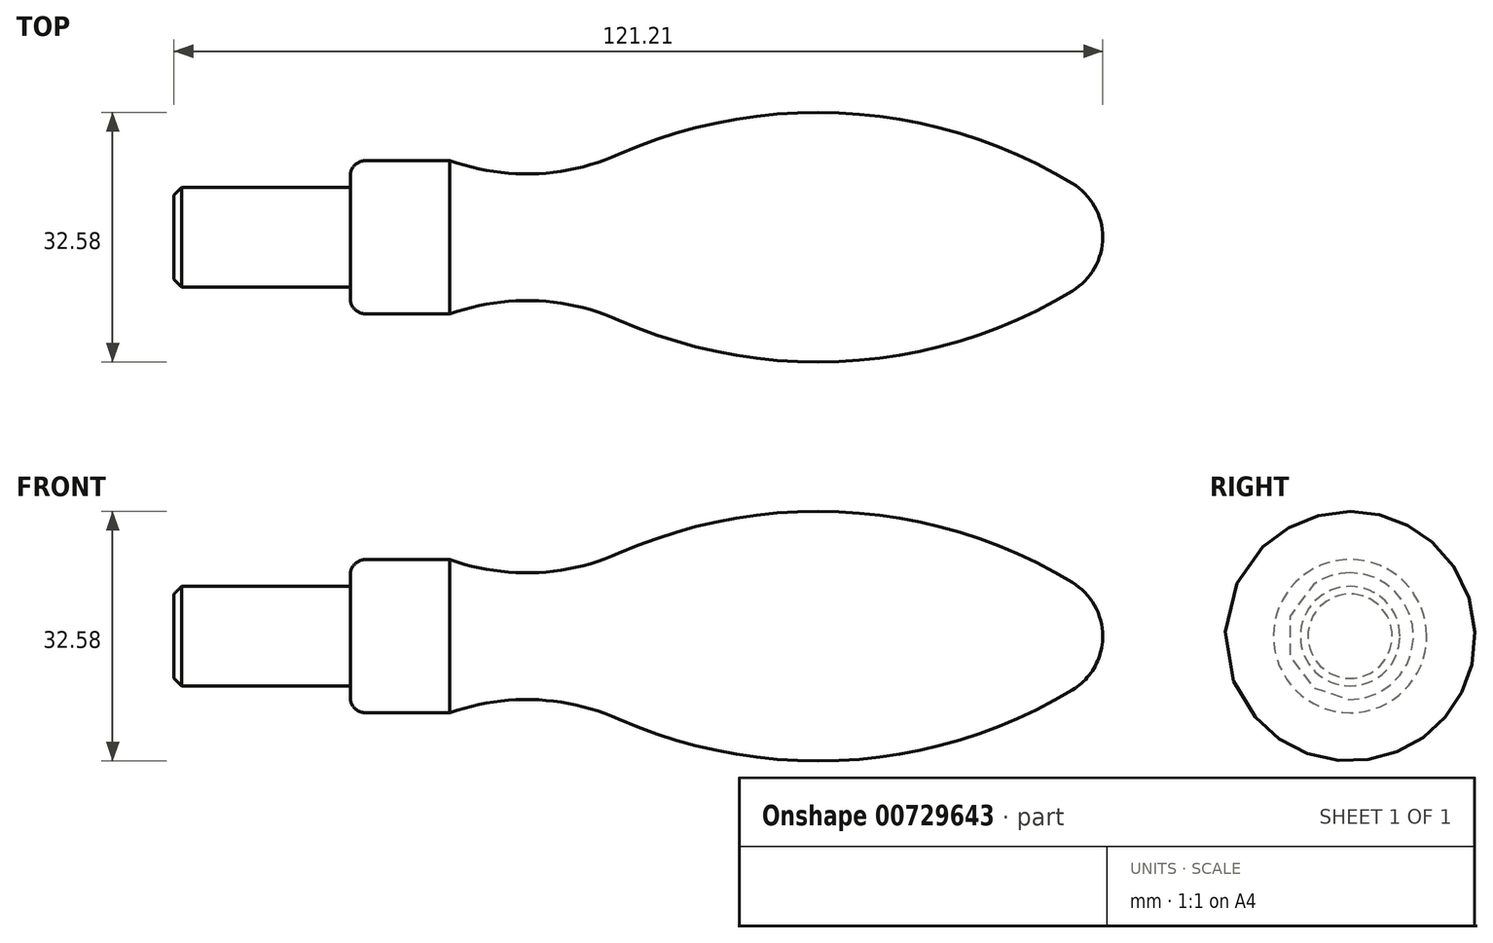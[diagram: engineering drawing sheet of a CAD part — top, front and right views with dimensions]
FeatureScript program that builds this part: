
annotation { "Feature Type Name" : "Feature", "Feature Type Description" : "" }
export const myFeature = defineFeature(function(context is Context, id is Id, definition is map)
    precondition{}
    {
        {
            var Q0;
            Q0=qCreatedBy(makeId("Front.planeOp"),FACE);
            var sketch = newSketch(context, id + "F0", { "sketchPlane" : qUnion([Q0])});
            skLineSegment(sketch, "E0", {"start": v(-68.37, 0) * mm, "end": v(0, 0) * mm, "construction": true});
            skLineSegment(sketch, "E1", {"start": v(0, 0) * mm, "end": v(23, -38) * mm, "construction": true});
            skLineSegment(sketch, "E2", {"start": v(0, 0) * mm, "end": v(0, -10) * mm});
            skLineSegment(sketch, "E3", {"start": v(0, -10) * mm, "end": v(13, -10) * mm});
            skLineSegment(sketch, "E4", {"start": v(61, 0) * mm, "end": v(61, 47.98) * mm, "construction": true});
            skLineSegment(sketch, "E5", {"start": v(90, 0) * mm, "end": v(90, 26.15) * mm, "construction": true});
            skArc(sketch, "E6", {"start": v(35.02, -10.8) * mm, "mid": v(24.09, -8.29) * mm, "end": v(13, -10) * mm});
            skArc(sketch, "E7", {"start": v(35.02, -10.8) * mm, "mid": v(65.1, -16.16) * mm, "end": v(94.25, -7.02) * mm});
            skArc(sketch, "E8", {"start": v(94.25, -7.02) * mm, "mid": v(97.15, -4.03) * mm, "end": v(98.2, 0) * mm});
            skLineSegment(sketch, "E9", {"start": v(0, 0) * mm, "end": v(98.2, 0) * mm, "construction": true});
            skLineSegment(sketch, "E10", {"start": v(0, 0) * mm, "end": v(98.2, 0) * mm});
            skSolve(sketch);
        }
        {
            var Q0;
            Q0 = qSketchRegion(id + "F0", true);
            var Q1;
            Q1=sQuery(id+"F0.wireOp",EDGE,"E0");
            revolve(context, id + "F1", {"surfaceOperationType" : NewSurfaceOperationType.NEW, "entities" : qUnion([Q0]), "axis" : qUnion([Q1]), "revolveType" : RevolveType.FULL});
        }
        {
            var Q0;
            Q0=makeQuery(id+"F1.opRevolve","SWEPT_FACE",FACE,{"disambiguationData":[OSD([sQuery(id+"F0.wireOp",EDGE,"E2")])]});
            var sketch = newSketch(context, id + "F2", { "sketchPlane" : qUnion([Q0])});
            skCircle(sketch, "E11", {"center": v(0, 0) * mm, "radius": 6.5 * mm});
            skSolve(sketch);
        }
        {
            var Q0;
            Q0 = qSketchRegion(id + "F2", true);
            extrude(context, id + "F3", {"entities" : qUnion([Q0]), "operationType" : NewBodyOperationType.ADD, "depth" : 23 * mm, "offsetDistance" : 25 * mm});
        }
        {
            var Q0;
            Q0=makeQuery(id+"F3.opExtrude","CAP_EDGE",EDGE,{"disambiguationData":[OSD([sQuery(id+"F2.wireOp",EDGE,"E11")])],"isStart":false});
            chamfer(context, id + "F4", {"entities" : qUnion([Q0]), "width" : 1 * mm, "tangentPropagation" : true});
        }
        {
            var Q0;
            Q0=makeQuery(id+"F1.opRevolve","SWEPT_EDGE",EDGE,{"disambiguationData":[OSD([sQuery(id+"F0.wireOp",EDGE,"E2"),sQuery(id+"F0.wireOp",EDGE,"E3")])]});
            fillet(context, id + "F5", {"entities" : qUnion([Q0]), "radius" : 2 * mm, "tangentPropagation" : true, "allowEdgeOverflow" : false});
        }
    });
